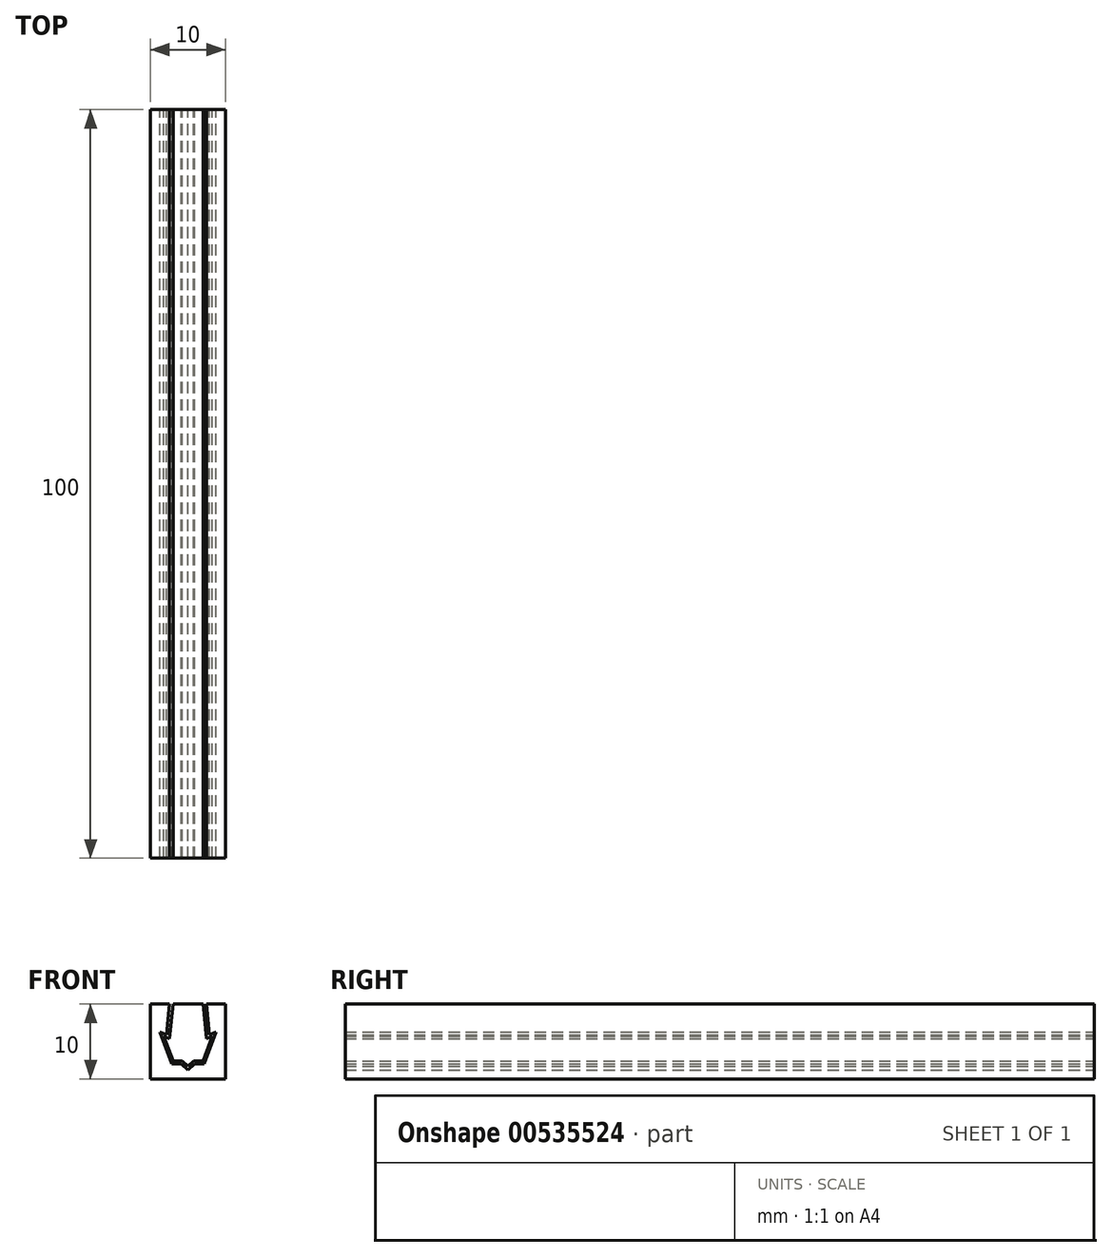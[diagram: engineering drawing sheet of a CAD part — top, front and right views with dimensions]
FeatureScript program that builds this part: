
annotation { "Feature Type Name" : "Feature", "Feature Type Description" : "" }
export const myFeature = defineFeature(function(context is Context, id is Id, definition is map)
    precondition{}
    {
        {
            var Q0;
            Q0=qCreatedBy(makeId("Front.planeOp"),FACE);
            var sketch = newSketch(context, id + "F0", { "sketchPlane" : qUnion([Q0])});
            skLineSegment(sketch, "E0.bottom", {"start": v(5, -5) * mm, "end": v(-5, -5) * mm});
            skLineSegment(sketch, "E0.top", {"start": v(5, 5) * mm, "end": v(-5, 5) * mm});
            skLineSegment(sketch, "E0.left", {"start": v(5, -5) * mm, "end": v(5, 5) * mm});
            skLineSegment(sketch, "E0.right", {"start": v(-5, -5) * mm, "end": v(-5, 5) * mm});
            skPoint(sketch, "E0.middle", {"position": v(0, 0) * mm});
            skLineSegment(sketch, "E1.bottom", {"start": v(-3, 5) * mm, "end": v(3, 5) * mm});
            skLineSegment(sketch, "E1.top", {"start": v(-2.18, -3) * mm, "end": v(-0.9, -3) * mm});
            skLineSegment(sketch, "E2", {"start": v(-0.9, -3) * mm, "end": v(0, -3.82) * mm});
            skPoint(sketch, "E2.endSnap0", {"position": v(0, -3) * mm});
            skLineSegment(sketch, "E3", {"start": v(0, -3.82) * mm, "end": v(0.9, -3) * mm});
            skLineSegment(sketch, "E4.trimOffspring", {"start": v(0.9, -3) * mm, "end": v(2.18, -3) * mm});
            skLineSegment(sketch, "E5.3", {"start": v(0.75, -2.6) * mm, "end": v(2, -2.6) * mm});
            skLineSegment(sketch, "E5.4", {"start": v(0, -3.28) * mm, "end": v(0.75, -2.6) * mm});
            skLineSegment(sketch, "E5.5", {"start": v(-0.75, -2.6) * mm, "end": v(0, -3.28) * mm});
            skLineSegment(sketch, "E5.9", {"start": v(-2, -2.6) * mm, "end": v(-0.75, -2.6) * mm});
            skLineSegment(sketch, "E6", {"start": v(-2.46, 0.39) * mm, "end": v(-2, 5) * mm});
            skLineSegment(sketch, "E7", {"start": v(-2, 5) * mm, "end": v(0, 5) * mm});
            skLineSegment(sketch, "E8", {"start": v(0, 5) * mm, "end": v(2, 5) * mm});
            skLineSegment(sketch, "E9", {"start": v(-2.89, 0.88) * mm, "end": v(-2.47, 5) * mm});
            skPoint(sketch, "E10.orphan", {"position": v(2.6, -2.6) * mm});
            skPoint(sketch, "E11.orphan", {"position": v(-2.6, -2.6) * mm});
            skLineSegment(sketch, "E12", {"start": v(5, -1.52) * mm, "end": v(10.66, -1.52) * mm});
            skPoint(sketch, "E13.start.orphan", {"position": v(1.68, -2.6) * mm});
            skPoint(sketch, "E14.orphan", {"position": v(3, -3) * mm});
            skPoint(sketch, "E15.orphan", {"position": v(-3, -3) * mm});
            skPoint(sketch, "E16.orphan", {"position": v(-4.2, -1.52) * mm});
            skPoint(sketch, "E17.center.orphan", {"position": v(-3, 0) * mm});
            skPoint(sketch, "E18.center.orphan", {"position": v(3, 0) * mm});
            skLineSegment(sketch, "E19", {"start": v(-2.89, 0.88) * mm, "end": v(-3.76, 1.28) * mm});
            skLineSegment(sketch, "E20", {"start": v(-3.76, 1.28) * mm, "end": v(-2.18, -3) * mm});
            skLineSegment(sketch, "E21", {"start": v(-2.46, 0.39) * mm, "end": v(-3.23, 0.72) * mm});
            skLineSegment(sketch, "E22", {"start": v(-3.23, 0.72) * mm, "end": v(-2, -2.6) * mm});
            skPoint(sketch, "E23.orphan", {"position": v(-2.49, -0.45) * mm});
            skPoint(sketch, "E5.8.end.orphan", {"position": v(-2.54, -1.52) * mm});
            skPoint(sketch, "E5.2.start.orphan", {"position": v(2.6, -0.45) * mm});
            skPoint(sketch, "E24.end.orphan", {"position": v(2.6, -1.52) * mm});
            skLineSegment(sketch, "E25.MirrorCS", {"start": v(2.46, 0.39) * mm, "end": v(2, 5) * mm});
            skLineSegment(sketch, "E26.MirrorCS", {"start": v(2.89, 0.88) * mm, "end": v(2.47, 5) * mm});
            skLineSegment(sketch, "E27.MirrorCS", {"start": v(2.89, 0.88) * mm, "end": v(3.76, 1.28) * mm});
            skLineSegment(sketch, "E28.MirrorCS", {"start": v(2.46, 0.39) * mm, "end": v(3.23, 0.72) * mm});
            skLineSegment(sketch, "E29.MirrorCS", {"start": v(3.76, 1.28) * mm, "end": v(2.18, -3) * mm});
            skLineSegment(sketch, "E30.MirrorCS", {"start": v(3.23, 0.72) * mm, "end": v(2, -2.6) * mm});
            skSolve(sketch);
        }
        {
            var Q0;
            {var subQ10=sQuery(id+"F0.wireOp",EDGE,"E0.bottom");Q0=makeQuery(id+"F0.imprint","IMPRINT",FACE,{"disambiguationData":[TD([[makeQuery(id+"F0.imprint","IMPRINT",EDGE,{"derivedFrom":subQ10}),-1.0]])]});}
            extrude(context, id + "F1", {"entities" : qUnion([Q0]), "depth" : 100 * mm, "offsetDistance" : 25 * mm});
        }
        {
            var Q0;
            Q0=makeQuery(id+"F0.imprint","IMPRINT",FACE,{"disambiguationData":[TD([[makeQuery(id+"F0.imprint","IMPRINT",EDGE,{"derivedFrom":sQuery(id+"F0.wireOp",EDGE,"E5.3")}),1.0]])]});
            extrude(context, id + "F2", {"entities" : qUnion([Q0]), "depth" : 100 * mm, "offsetDistance" : 25 * mm});
        }
    });
